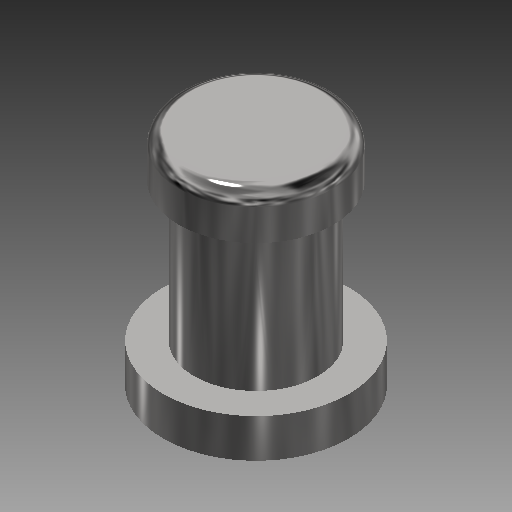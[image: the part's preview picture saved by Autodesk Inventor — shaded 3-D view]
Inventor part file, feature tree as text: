
AUTODESK INVENTOR PART (.ipt)
format: ipt  version: 2019 (Build 230136000, 136)  size: 155,648 bytes
history: native  units: mm
features: revolve x1, sketch x1
ambient origin geometry x8: Origin, YZ Plane, XZ Plane, XY Plane, X Axis, Y Axis, Z Axis, Center Point
bodies: Solid1 (feature_tree)
feature tree (2):
  revolve  "Revolution1"  [1 undecoded]
  sketch  "Sketch1"  dims[d1=10.0mm d2=8.0mm d3=12.0mm d4=9.0mm d5=3.0mm d6=2.5mm d7=1.0mm d8=90.0deg]
note: 1 required parameter value undecoded (feature->parameter linkage not recoverable at this tier; creation-order binding heuristic only, values carry confidence <= 0.55)
